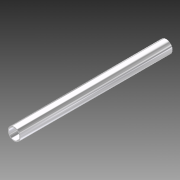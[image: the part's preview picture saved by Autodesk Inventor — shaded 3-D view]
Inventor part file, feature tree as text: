
AUTODESK INVENTOR PART (.ipt)
format: ipt  version: 2011 (Build 150239000, 239)  size: 72,192 bytes
history: native  units: in
note: dims shown in document units (in); Inventor stores cm internally (conversion verified against a paired STEP export)
features: extrude x1, sketch x1
ambient origin geometry x8: Origin, YZ Plane, XZ Plane, XY Plane, X Axis, Y Axis, Z Axis, Center Point
bodies: Solid1 (feature_tree)
feature tree (2):
  extrude  "Extrusion1"  Depth=0.95in
  sketch  "Sketch1"  dims[d0=1.125in d1=0.95in d2=13.5in d3=0.0in]
